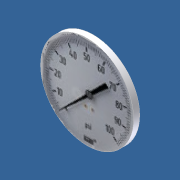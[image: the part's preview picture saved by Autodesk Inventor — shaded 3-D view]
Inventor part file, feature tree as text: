
AUTODESK INVENTOR PART (.ipt)
format: ipt  version: unknown  size: 199,680 bytes
history: native  units: in
note: dims shown in document units (in); Inventor stores cm internally (conversion verified against a paired STEP export)
features: other x2, sketch x2, extrude x1
ambient origin geometry x8: Origin, YZ Plane, XZ Plane, XY Plane, X Axis, Y Axis, Z Axis, Center Point
bodies: Solid1 (feature_tree)
feature tree (5):
  extrude  "Extrusion1"  Depth=0.1in TaperAngle=0.0deg
  other  "Decal1"
  sketch  "Sketch1"  dims[d0=1.525in d1=0.1in d2=0.0in]
  sketch  "Sketch2"
  other  "Image2"
